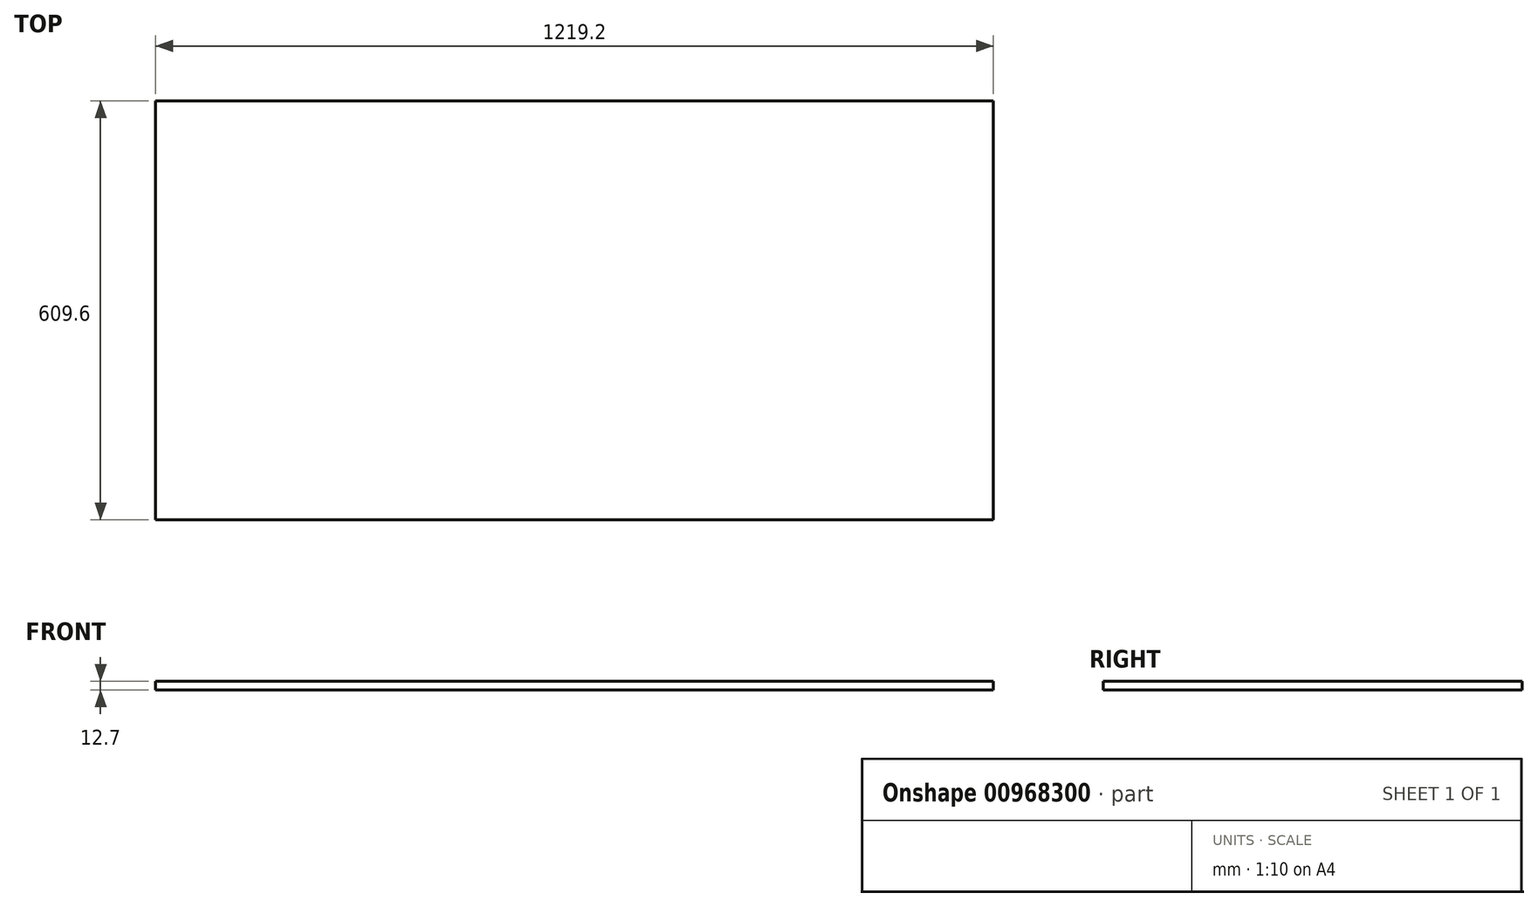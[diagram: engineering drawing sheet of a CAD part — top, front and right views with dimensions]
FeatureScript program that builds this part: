
annotation { "Feature Type Name" : "Feature", "Feature Type Description" : "" }
export const myFeature = defineFeature(function(context is Context, id is Id, definition is map)
    precondition{}
    {
        {
            var Q0;
            Q0=qCreatedBy(makeId("Top.planeOp"),FACE);
            var sketch = newSketch(context, id + "F0", { "sketchPlane" : qUnion([Q0])});
            skLineSegment(sketch, "E0.bottom", {"start": v(609.6, 304.8) * mm, "end": v(-609.6, 304.8) * mm});
            skLineSegment(sketch, "E0.top", {"start": v(609.6, -304.8) * mm, "end": v(-609.6, -304.8) * mm});
            skLineSegment(sketch, "E0.left", {"start": v(609.6, 304.8) * mm, "end": v(609.6, -304.8) * mm});
            skLineSegment(sketch, "E0.right", {"start": v(-609.6, 304.8) * mm, "end": v(-609.6, -304.8) * mm});
            skPoint(sketch, "E0.middle", {"position": v(0, 0) * mm});
            skSolve(sketch);
        }
        {
            var Q0;
            Q0 = qSketchRegion(id + "F0", true);
            extrude(context, id + "F1", {"entities" : qUnion([Q0]), "depth" : 12.7 * mm, "offsetDistance" : 25.4 * mm});
        }
    });
